# Revit family: QF_BPRO_BLT 1020 EB_572519
name_source: partatom
category: Sonderausstattung
revit_build: Autodesk Revit 2018 (Build: 20190510_1515(x64)
units: mm (PartAtom-declared; Revit-internal decimal feet)

## family parameters
Arbeitsebenenbasiert = Nein
Beim Laden mit Abzugskörper schneiden = Nein
Bemaßung runder Anschluss = Durchmesser verwenden
Gemeinsam genutzt = Nein
Immer vertikal = Ja
Raumberechnungspunkt = Ja
Teiletyp = Normal

## types (1)
- BLT 1020 EB
    Artikel Nummer = 572519
    Beschreibung = B.PROTHERM 1020 EB  Speisentransportbehälter  aus rostfreiem Edelstahl,
umluftbeheizt,  mit Flügeltür, fahrbar
Kapazität: GN-Behälter bis max.  3x GN 1/1-200 + 1x GN 1/1-100
Anzahl Auflagensicken: 14 Paar Auflagesicken
Sickenabstand: 57,5 mm
    Beschreibung durch Hersteller analog Leistungsverzeichniskurztext = Abmessungen

Länge:			540 mm
Breite:			815 mm
Höhe:			1.150 mm


Ausführung

Aufbau
Der Speisentransportbehälter besteht aus CNS 18/10, Werkstoff-Nr. 1.4301. Die Oberfläche ist mikroliert.  
Behälter und Flügeltür sind doppelwandig und mit FCKW-freiem PUR-Schaum temperaturisolierend ausgeschäumt. Das Heizmodul mit Umluftheizung ist in die Tür eingesetzt. Der Behälter ist fahrbar mittels rostfreien Kunststoffrollen gemäß DIN 18867, Teil 8 (2 Bock- und 2 Lenkrollen mit Feststeller, Rollendurchmesser 125 mm). Die stabile Bodenkonstruktion aus Kunststoff mit integriertem, umlaufendem Stoßschutz schützt Gerät und Mobiliar vor Beschädigung.

Korpus
Die geschlossene Abdeckung des BLT 1020 EB ist mit Stapelprägungen versehen, die die Stapelfähigkeit mit B.PROTHERM-Behältern aus Kunststoff erlauben.

Boden-, Rücken- und Seitenwände sind fugenlos verschweißt mit Kantradien R3 (Hygieneausführung H1). Die Seitenwände sind mit 14 Paar tiefgezogenen Auflagesicken im Abstand von 57,5mm zur Aufnahme von Gastronorm-Behältern der Größe GN 1/1 oder deren Unterteilung versehen. An der Rückwand des Innenkorpus befinden sich ebenfalls im Abstand von 57,5 mm Prägungen, die auch bei Bestückung mit GN-Behältern ein Zirkulieren der Heißluft und somit eine gleichmäßige Temperatur im  Behälterinnenraum ermöglichen. 
Innenkorpus mit Außenkorpus frontseitig wasserdicht verschweißt.

Der Behälter ist frontseitig mit einer um 180° schwenkbaren, bei Bedarf abnehmbaren Flügeltür ausgestattet. Tür innen mit entnehmbarem, umlaufendem und lebensmittelbeständigem Dichtungsrahmen. 
In die Tür eingesetzt das Heizmodul mit Umluftheizung. Das Heizmodul kann zu Reinigungszwecken entnommen werden. Heizmodul steckerfertig mit separatem Ein/Aus-Schalter, Temperaturregler, Spiralkabel und Blindsteckerbuchse. Regelbereich: +30°C bis +90°C. Die Temperatur ist stufenlos regelbar. Das Heizmodul ist durch seine charakteristische, nach unten schräg abfallende Form leicht bedien- und ablesbar.
Tür außen mit robuster Spannverschlussleiste aus CNS. In die Tür eingebaut sind eine analoge Temperaturanzeige sowie eine Feuchtigkeits-regulierung für den Behälterinnenraum.
Die Tür ist frontseitig mit einem CNS-Sicherheits-Schiebegriff mit seitlichen Stoßschutzelementen aus Kunststoff (Polyamid) ausgestattet. Der ergonomische Schiebegriff bietet zusätzliche Schutzfunktion für die darunter liegenden Bedienelemente. 

Stabile, geschlossene Bodenkonstruktion aus massivem Kunststoff mit integriertem, umlaufendem Stoßschutz.

Der Korpus ist frontseitig mit einer Kondensat-auffangrinne aus Kunststoff (Polyamid) ausgestattet, zur Vermeidung von Rutsch- und Verletzungsgefahr.

Alle Verschleißteile (wie z.B. Rollen, Schiebegriff, Verschlüsse etc.) sind im Servicefall einfach austauschbar. 


Zubehör/ Optionen

•	Zusätzlicher Stoßschutz am Dach aus massivem Kunststoff (analog Bodenplatte)
•	Dach (glatt) mit umlaufender Galerie aus CNS
•	Zusätzlicher Schiebegriff an der Geräterückseite
•	Tür nicht aushängbar
•	Eutektische Platte -3°C, aus Kunststoff (Best.Nr. 568 136)
•	Eutektische Platte -12°C, aus Kunststoff (Best.Nr. 573 332)
•	Einschubrahmen zur Unterteilung von GN-Behältern mit max. Tiefe 150 mm  (Best.Nr. 564 352)
•	GN-Stege zum variablen Einsetzen von GN-Behältern der Größe GN 1/4, GN 1/6, GN 1/9 in den Einschubrahmen (ST 3 Best.Nr. 550 650, 
ST 5 Best.Nr. 550 651)
•	Menükarten-Halterung an Tür frontseitig zur Aufnahme von Menükarten DIN A 6
•	BLT E-Menükarte mit Schlüssellochung, DIN A 6 (Best.Nr. 572 513) 
•	Spezialstift, zur Beschriftung der BLT E-Menükarten              (Best.Nr. 564 361)
•	Menükarten-Box, Kunststoff (Best.Nr. 564 355)
•	Weitere Rollenoptionen siehe Gesamtpreisliste


Technische Daten

Werkstoff:	Chromnickelstahl 18/10,
	                        Kunststoff (PA, PE-HD)
Isoliermaterial:	PUR-Schaum - FCKW-frei 
Gewicht:	                        65 kg
Kapazität:	max. 3x GN 1/1-200 + 1x GN  1/1-100
Sicken:	                        14 Paar Auflagesicken, Sickenabstand 57,5 mm
Anschlusswert:	220-240V AC/ 50-60Hz/ 
		0,76kW
Temperaturbereich:	+30°C - +90°C*
Emissionen:	Der arbeitsplatzbezogene 
	                        Schallpegel des Geräts ist
	                        kleiner als 70 dB(A)

* gemessen im geometrischen Mittelpunkt des Behälters


Besonderheit

•	wasserdichter Innenkorpus in Hygieneausführung H1, Kantradien R3
•	Rückwand Innenkorpus mit Prägungen für optimale Heißluftzirkulation
•	Korpus frontseitig mit Kondensat-Auffangrinne
•	Schutzart IP X5 (Schutz vor Strahlwasser)


Fabrikat

Hersteller:      B.PRO
Modell:	        BLT 1020 EB
	        B.PROTHERM
Best.Nr.	        572 519
    Beschreibung durch Hersteller analog Leistungsverzeichnislangtext = Abmessungen

Länge:			540 mm
Breite:			815 mm
Höhe:			1.150 mm


Ausführung

Aufbau
Der Speisentransportbehälter besteht aus CNS 18/10, Werkstoff-Nr. 1.4301. Die Oberfläche ist mikroliert.  
Behälter und Flügeltür sind doppelwandig und mit FCKW-freiem PUR-Schaum temperaturisolierend ausgeschäumt. Das Heizmodul mit Umluftheizung ist in die Tür eingesetzt. Der Behälter ist fahrbar mittels rostfreien Kunststoffrollen gemäß DIN 18867, Teil 8 (2 Bock- und 2 Lenkrollen mit Feststeller, Rollendurchmesser 125 mm). Die stabile Bodenkonstruktion aus Kunststoff mit integriertem, umlaufendem Stoßschutz schützt Gerät und Mobiliar vor Beschädigung.

Korpus
Die geschlossene Abdeckung des BLT 1020 EB ist mit Stapelprägungen versehen, die die Stapelfähigkeit mit B.PROTHERM-Behältern aus Kunststoff erlauben.

Boden-, Rücken- und Seitenwände sind fugenlos verschweißt mit Kantradien R3 (Hygieneausführung H1). Die Seitenwände sind mit 14 Paar tiefgezogenen Auflagesicken im Abstand von 57,5mm zur Aufnahme von Gastronorm-Behältern der Größe GN 1/1 oder deren Unterteilung versehen. An der Rückwand des Innenkorpus befinden sich ebenfalls im Abstand von 57,5 mm Prägungen, die auch bei Bestückung mit GN-Behältern ein Zirkulieren der Heißluft und somit eine gleichmäßige Temperatur im  Behälterinnenraum ermöglichen. 
Innenkorpus mit Außenkorpus frontseitig wasserdicht verschweißt.

Der Behälter ist frontseitig mit einer um 180° schwenkbaren, bei Bedarf abnehmbaren Flügeltür ausgestattet. Tür innen mit entnehmbarem, umlaufendem und lebensmittelbeständigem Dichtungsrahmen. 
In die Tür eingesetzt das Heizmodul mit Umluftheizung. Das Heizmodul kann zu Reinigungszwecken entnommen werden. Heizmodul steckerfertig mit separatem Ein/Aus-Schalter, Temperaturregler, Spiralkabel und Blindsteckerbuchse. Regelbereich: +30°C bis +90°C. Die Temperatur ist stufenlos regelbar. Das Heizmodul ist durch seine charakteristische, nach unten schräg abfallende Form leicht bedien- und ablesbar.
Tür außen mit robuster Spannverschlussleiste aus CNS. In die Tür eingebaut sind eine analoge Temperaturanzeige sowie eine Feuchtigkeits-regulierung für den Behälterinnenraum.
Die Tür ist frontseitig mit einem CNS-Sicherheits-Schiebegriff mit seitlichen Stoßschutzelementen aus Kunststoff (Polyamid) ausgestattet. Der ergonomische Schiebegriff bietet zusätzliche Schutzfunktion für die darunter liegenden Bedienelemente. 

Stabile, geschlossene Bodenkonstruktion aus massivem Kunststoff mit integriertem, umlaufendem Stoßschutz.

Der Korpus ist frontseitig mit einer Kondensat-auffangrinne aus Kunststoff (Polyamid) ausgestattet, zur Vermeidung von Rutsch- und Verletzungsgefahr.

Alle Verschleißteile (wie z.B. Rollen, Schiebegriff, Verschlüsse etc.) sind im Servicefall einfach austauschbar. 


Zubehör/ Optionen

•	Zusätzlicher Stoßschutz am Dach aus massivem Kunststoff (analog Bodenplatte)
•	Dach (glatt) mit umlaufender Galerie aus CNS
•	Zusätzlicher Schiebegriff an der Geräterückseite
•	Tür nicht aushängbar
•	Eutektische Platte -3°C, aus Kunststoff (Best.Nr. 568 136)
•	Eutektische Platte -12°C, aus Kunststoff (Best.Nr. 573 332)
•	Einschubrahmen zur Unterteilung von GN-Behältern mit max. Tiefe 150 mm  (Best.Nr. 564 352)
•	GN-Stege zum variablen Einsetzen von GN-Behältern der Größe GN 1/4, GN 1/6, GN 1/9 in den Einschubrahmen (ST 3 Best.Nr. 550 650, 
ST 5 Best.Nr. 550 651)
•	Menükarten-Halterung an Tür frontseitig zur Aufnahme von Menükarten DIN A 6
•	BLT E-Menükarte mit Schlüssellochung, DIN A 6 (Best.Nr. 572 513) 
•	Spezialstift, zur Beschriftung der BLT E-Menükarten              (Best.Nr. 564 361)
•	Menükarten-Box, Kunststoff (Best.Nr. 564 355)
•	Weitere Rollenoptionen siehe Gesamtpreisliste


Technische Daten

Werkstoff:	Chromnickelstahl 18/10,
	                        Kunststoff (PA, PE-HD)
Isoliermaterial:	PUR-Schaum - FCKW-frei 
Gewicht:	                        65 kg
Kapazität:	max. 3x GN 1/1-200 + 1x GN  1/1-100
Sicken:	                        14 Paar Auflagesicken, Sickenabstand 57,5 mm
Anschlusswert:	220-240V AC/ 50-60Hz/ 
		0,76kW
Temperaturbereich:	+30°C - +90°C*
Emissionen:	Der arbeitsplatzbezogene 
	                        Schallpegel des Geräts ist
	                        kleiner als 70 dB(A)

* gemessen im geometrischen Mittelpunkt des Behälters


Besonderheit

•	wasserdichter Innenkorpus in Hygieneausführung H1, Kantradien R3
•	Rückwand Innenkorpus mit Prägungen für optimale Heißluftzirkulation
•	Korpus frontseitig mit Kondensat-Auffangrinne
•	Schutzart IP X5 (Schutz vor Strahlwasser)


Fabrikat

Hersteller:      B.PRO
Modell:	        BLT 1020 EB
	        B.PROTHERM
Best.Nr.	        572 519
    CE Kennzeichnung = Ja
    Elektrische leistung = 760 W
    Frequenz = 50 Hz
    Gerätegewicht Netto = 64.80 kg
    Großküchengerätezuordnung = Ja
    Hauptschalter integriert = Ja
    Hersteller = B.PRO GmbH
    Höhe = 1150 mm
    Internetadresse Gerätehersteller = https://www.bpro-solutions.com
    Internetadresse für Ersatzteilliste = https://www.bpro-solutions.com
    Kosten = 4379.7 $
    Länge Gerätebreite = 540 mm
    Material = QF_Metal-Stainless-Steel_general
    Modell = BLT 1020 EB
    Schalldruckpegel = < 70 dB(A)
    Sockelhöhe = 161 mm
    Spannung = 220 V
    Stecker System = Schuko Stecker
    Tiefe = 815 mm
    Typenkommentare = Speisetransportbehälter beheizt
    URL = https://www.bpro-solutions.com
    Warnhinweise = Mögliche Beeinträchtigung der Lebensmittelqualität:
Durch Stromausfall, Gerätestörungen oder sonstige Unterbrechungen während der Lagerung oder Regeneration kann die Qualität der im Gerät befindlichen Lebensmittel beeinträchtigt worden sein.
 -  Nach Absinken der Kerntemperatur prüfen, ob die Qualität der Lebensmittel
beeinträchtigt ist, Lebensmittel ggf. entsorgen.

Betrieb des Umluftheizmoduls:
Das Umluftheizmodul darf nur in eingebautem Zustand in Kombination mit dem BLANCOTHERM Edelstahl, beheizt betrieben werden

Beschickung:
Gerät nur mit abgedeckelten Gastronormbehältern beschicken.
Im Gerät eingesetzte Gastronormbehälter müssen bis zu einer Temperatur
von mindestens +100 °C hitzebeständig sein. Beispielsweise dürfen keine Gastronormbehälter aus Polycarbonat verwendet werden.
Um eine Verlagerung des Schwerpunkts zur Geräteoberseite zu vermeiden, Gerät bei Teilbeschickung von unten nach oben beschicken.
Die in den technischen Daten angegebenen Gewichtsobergrenzen bei der
Zuladung dürfen nicht überschritten werden.

Heißes Umluftheizmodul, heiße Geräteteile, Gegenstände und Speisen:
Das Umluftheizmodul, der Geräteinnenraum und darin enthaltene Gegenstände (z. B. Gastronormbehälter) werden bei Betrieb heiß (bis ca. +90 °C) und können Verbrennungen verursachen. Heiße Teile nur geschützt (z. B. mit
Topflappen oder Schutzhandschuhen) anfassen.
Die warmgehaltenen Speisen können Verbrühungen verursachen.

Warme Geräteaußenseite:
Die Geräteaußenseite wird bei Betrieb warm. Keine wärmeempfindlichen Gegenstände oder Speisen auf die Geräteoberseite stellen.

Ausführliche Gefahrenhinweise entnehmen Sie der Betriebsanleitung.
    Zubehör = Ja
    Zuleitung zum Gerät im Lieferumfang = Ja
